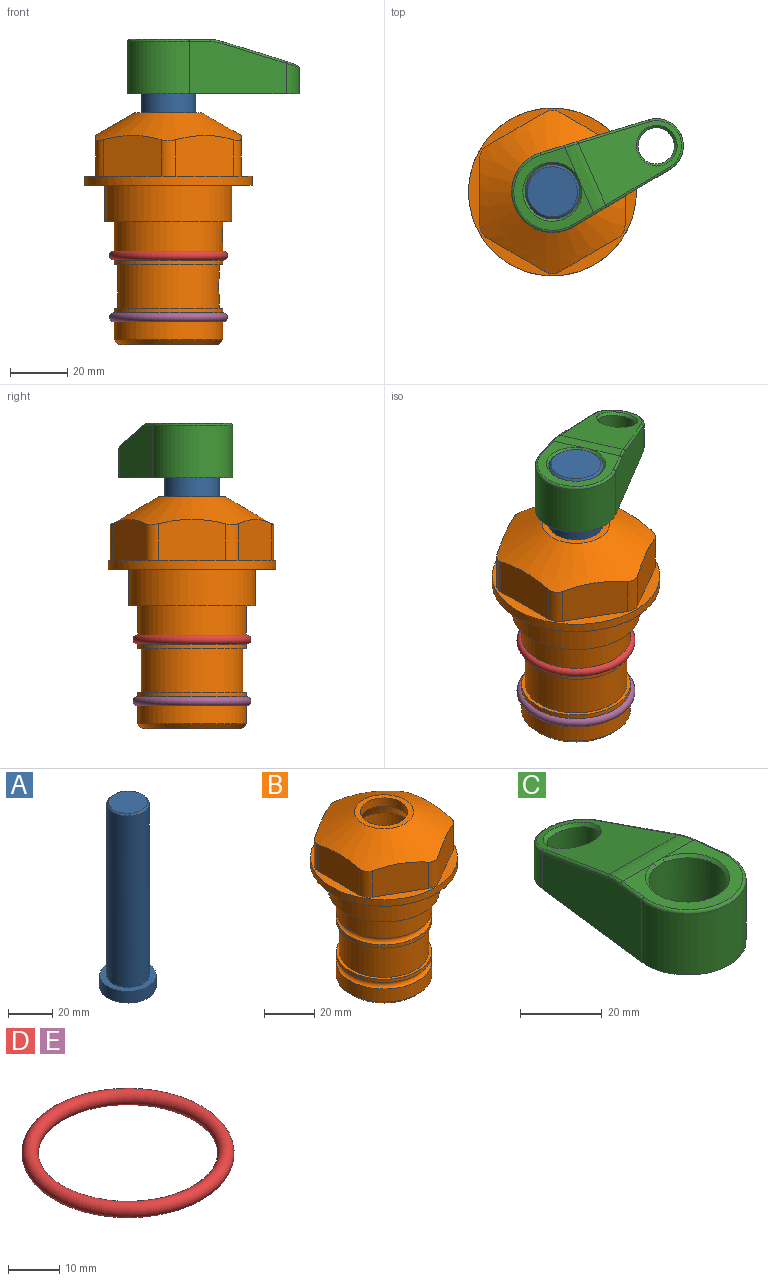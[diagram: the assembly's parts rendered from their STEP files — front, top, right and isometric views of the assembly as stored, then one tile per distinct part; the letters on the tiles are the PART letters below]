
ASSEMBLY  parts=5 mates=4
PART A: 6 faces, bbox 25.4x25.4x101.6 mm
  f0: plane 17.46x17.46mm, normal (0,0,1), area 239.5mm2, adj f5
  f1: plane 25.4x25.4mm, normal (0,0,-1), area 506.7mm2, adj f2
  f2: cylinder r=12.7mm len=25.4mm, axis (0,0,1), area 506.7mm2, adj f1,f3
  f3: plane 25.4x25.4mm, normal (0,0,1), area 221.7mm2, adj f2,f4
  f4: cylinder r=9.53mm len=94.46mm, axis (0,0,1), area 5653mm2, adj f3,f5
  f5: cone r=8.73mm half-angle=45deg, axis (0,0,-1), area 64.4mm2, adj f0,f4
PART B: 36 faces, bbox 58.7x58.7x81 mm
  f0: cylinder r=17.78mm len=35.56mm, axis (0,0,1), area 1670.8mm2, adj f23,f24,f31
  f1: cylinder r=19.05mm len=38.1mm, axis (0,0,1), area 1191.9mm2, adj f26,f27,f30
  f2: plane 58.66x58.66mm, normal (0,0,-1), area 1150.6mm2, adj f3,f28
  f3: cylinder r=29.33mm len=58.66mm, axis (0,0,-1), area 585.1mm2, adj f2,f4
  f4: plane 58.66x58.66mm, normal (0,0,1), area 475.9mm2, adj f3,f5,f6,f7,f8,f9,f10,f11
  f5: plane 20.32x14.34mm, normal (-0.5,0.87,0), area 324.4mm2, adj f4,f15,f16,f17
  f6: plane 20.32x14.34mm, normal (0.5,0.87,0), area 324.4mm2, adj f4,f14,f15,f17
  f7: plane 23.48x14.34mm, normal (1,0,0), area 324.4mm2, adj f4,f13,f14,f17
  f8: plane 20.32x14.34mm, normal (0.5,-0.87,0), area 324.4mm2, adj f4,f12,f13,f17
  f9: plane 20.32x14.34mm, normal (-0.5,-0.87,0), area 324.4mm2, adj f4,f11,f12,f17
  f10: plane 23.48x14.34mm, normal (-1,0,0), area 324.4mm2, adj f4,f11,f16,f17
  f11: cylinder r=5.08mm len=12.85mm, axis (0,0,-1), area 67.2mm2, adj f4,f9,f10,f17
  f12: cylinder r=5.08mm len=12.85mm, axis (0,0,-1), area 67.2mm2, adj f4,f8,f9,f17
  f13: cylinder r=5.08mm len=12.85mm, axis (0,0,-1), area 67.2mm2, adj f4,f7,f8,f17
  f14: cylinder r=5.08mm len=12.85mm, axis (0,0,-1), area 67.2mm2, adj f4,f6,f7,f17
  f15: cylinder r=5.08mm len=12.85mm, axis (0,0,-1), area 67.2mm2, adj f4,f5,f6,f17
  f16: cylinder r=5.08mm len=12.85mm, axis (0,0,-1), area 67.2mm2, adj f4,f5,f10,f17
  f17: cone r=11.73mm half-angle=60deg, axis (0,0,-1), area 2071.8mm2, adj f5,f6,f7,f8,f9,f10,f11,f12
  f18: plane 23.46x23.46mm, normal (0,0,1), area 147.4mm2, adj f17,f35
  f19: plane 34.93x34.93mm, normal (0,0,-1), area 958mm2, adj f29
  f20: cylinder r=19.05mm len=38.1mm, axis (0,0,1), area 760.1mm2, adj f21,f29
  f21: torus R=19.05mm, axis (0,0,1), area 565.3mm2, adj f20,f22
  f22: cylinder r=19.05mm len=38.1mm, axis (0,0,1), area 190mm2, adj f21,f23
  f23: plane 38.1x38.1mm, normal (0,0,1), area 146.9mm2, adj f0,f22
  f24: plane 38.1x38.1mm, normal (0,0,-1), area 146.9mm2, adj f0,f25
  f25: cylinder r=19.05mm len=38.1mm, axis (0,0,1), area 190mm2, adj f24,f26
  f26: torus R=19.05mm, axis (0,0,1), area 565.3mm2, adj f1,f25
  f27: plane 44.45x44.45mm, normal (0,0,-1), area 411.7mm2, adj f1,f28
  f28: cylinder r=22.23mm len=44.45mm, axis (0,0,1), area 1773.5mm2, adj f2,f27
  f29: cone r=19.05mm half-angle=45deg, axis (0,0,1), area 257.5mm2, adj f19,f20
  f30: cylinder r=3.17mm len=6.75mm, axis (-1,0,0), area 128mm2, adj f1,f33
  f31: cylinder r=3.17mm len=6.35mm, axis (-1,0,0), area 102.5mm2, adj f0,f33
  f32: plane 25.4x25.4mm, normal (0,0,1), area 506.7mm2, adj f33
  f33: cylinder r=12.7mm len=66.42mm, axis (0,0,-1), area 5236.2mm2, adj f30,f31,f32,f34
  f34: cone r=9.53mm half-angle=30deg, axis (0,0,-1), area 443.4mm2, adj f33,f35
  f35: cylinder r=9.53mm len=19.05mm, axis (0,0,-1), area 240.9mm2, adj f18,f34
PART C: 31 faces, bbox 31.7x65.5x19.8 mm
  f0: plane 39.12x18.26mm, normal (0.99,0.12,0), area 612.2mm2, adj f1,f4,f7,f11,f13,f15
  f1: cylinder r=9.53mm len=18.91mm, axis (0,0,-1), area 296.1mm2, adj f0,f2,f7,f17
  f2: plane 39.12x18.26mm, normal (-0.99,0.12,0), area 612.2mm2, adj f1,f4,f7,f12,f14,f16
  f3: cylinder r=6.35mm len=12.7mm, axis (0,0,-1), area 362.4mm2, adj f7,f18
  f4: cylinder r=14.29mm len=28.58mm, axis (0,0,-1), area 882.2mm2, adj f0,f2,f7,f10
  f5: cylinder r=9.53mm len=19.05mm, axis (0,0,-1), area 1092.6mm2, adj f7,f19,f20
  f6: plane 26.99x23.69mm, normal (0,0,1), area 216.2mm2, adj f9,f10,f11,f12,f19
  f7: plane 63.5x28.58mm, normal (0,0,-1), area 661.8mm2, adj f0,f1,f2,f3,f4,f5,f22,f23
  f8: plane 33.52x23.6mm, normal (0,0.26,0.97), area 486mm2, adj f9,f15,f16,f17,f18
  f9: cylinder r=19.05mm len=24.72mm, axis (1,0,0), area 120.4mm2, adj f6,f8,f13,f14,f20
  f10: torus R=13.49mm, axis (0,0,1), area 59mm2, adj f4,f6,f11,f12
  f11: cylinder r=0.79mm len=8.67mm, axis (0.12,-0.99,0), area 10.8mm2, adj f0,f6,f10,f13
  f12: cylinder r=0.79mm len=8.67mm, axis (0.12,0.99,0), area 10.8mm2, adj f2,f6,f10,f14
  f13: bspline ~4.95x1.42mm, area 6.1mm2, adj f0,f9,f11,f15
  f14: bspline ~4.95x1.42mm, area 6.1mm2, adj f2,f9,f12,f16
  f15: cylinder r=0.79mm len=25.95mm, axis (0.12,-0.96,0.26), area 32.9mm2, adj f0,f8,f13,f17
  f16: cylinder r=0.79mm len=25.95mm, axis (0.12,0.96,-0.26), area 32.9mm2, adj f2,f8,f14,f17
  f17: bspline ~18.91x8.38mm, area 30mm2, adj f1,f8,f15,f16
  f18: bspline ~14.29x14.29mm, area 48.3mm2, adj f3,f8
  f19: cone r=9.53mm half-angle=45deg, axis (0,0,1), area 66.5mm2, adj f5,f6,f20
  f20: bspline ~3.22x0.96mm, area 3.5mm2, adj f5,f9,f19
  f21: plane 2.75x2.72mm, normal (0,0,-1), area 2.9mm2, adj f23,f25,f28
  f22: plane 23.05x15.88mm, normal (-0.99,-0.12,0), area 323.6mm2, adj f7,f25,f26,f27,f28,f29
  f23: plane 23.05x15.88mm, normal (0.99,-0.12,0), area 323.6mm2, adj f7,f21,f25,f27,f28,f30
  f24: cylinder r=9.53mm len=10.69mm, axis (0,0,-1), area 114.7mm2, adj f7,f27,f29,f30
  f25: cylinder r=12.7mm len=20.59mm, axis (0,0,-1), area 381.1mm2, adj f7,f21,f22,f23,f26,f28
  f26: plane 2.75x2.72mm, normal (0,0,-1), area 2.9mm2, adj f22,f25,f28
  f27: plane 19.72x18.37mm, normal (0,-0.26,-0.97), area 291.8mm2, adj f22,f23,f24,f28,f29,f30
  f28: cylinder r=15.88mm len=19.92mm, axis (1,0,0), area 54.8mm2, adj f21,f22,f23,f25,f26,f27
  f29: cylinder r=1.59mm len=11mm, axis (0,0,-1), area 34.7mm2, adj f7,f22,f24,f27
  f30: cylinder r=1.59mm len=11mm, axis (0,0,-1), area 34.7mm2, adj f7,f23,f24,f27
PART D: 1 faces, bbox 44.7x44.7x3.2 mm
  f0: torus R=19.05mm, axis (0,0,1), area 1193.9mm2
PART E: same geometry as D
PLACE A rot(axis=(0,0,-1),66.1deg) t=(0,0,-12.45)mm
PLACE B at identity fixed
PLACE C rot(axis=(0,0,-1),66.1deg) t=(0,0,-12.45)mm
PLACE D at identity
PLACE E t=(0,0,-21.59)mm
MATE fastened B.f0 <-> D.f0  axis (0,0,1) through (0,0,-24.51)mm
MATE fastened E.f0 <-> B.f0  axis (0,0,1) through (0,0,-46.1)mm
MATE cylindrical A.f2 <-> B.f0  axis (0,0,-1) through (0,0,-50.55)mm
MATE fastened A.f2 <-> C.f4  axis (0,0,1) through (0,0,51.05)mm
